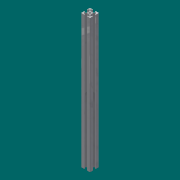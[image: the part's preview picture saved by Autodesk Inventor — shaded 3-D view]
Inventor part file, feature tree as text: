
AUTODESK INVENTOR PART (.ipt)
format: ipt  version: 2016 SP1 (Build 200210100, 210)  size: 148,992 bytes
history: native  units: mm
features: extrude x1, sketch x1
ambient origin geometry x8: Origin, YZ Plane, XZ Plane, XY Plane, X Axis, Y Axis, Z Axis, Center Point
bodies: Solid1 (feature_tree)
feature tree (2):
  extrude  "Extrusion1"  [1 undecoded]
  sketch  "Sketch1"  dims[d0=300.0mm d1=0.0mm]
note: 1 required parameter value undecoded (feature->parameter linkage not recoverable at this tier; creation-order binding heuristic only, values carry confidence <= 0.55)
